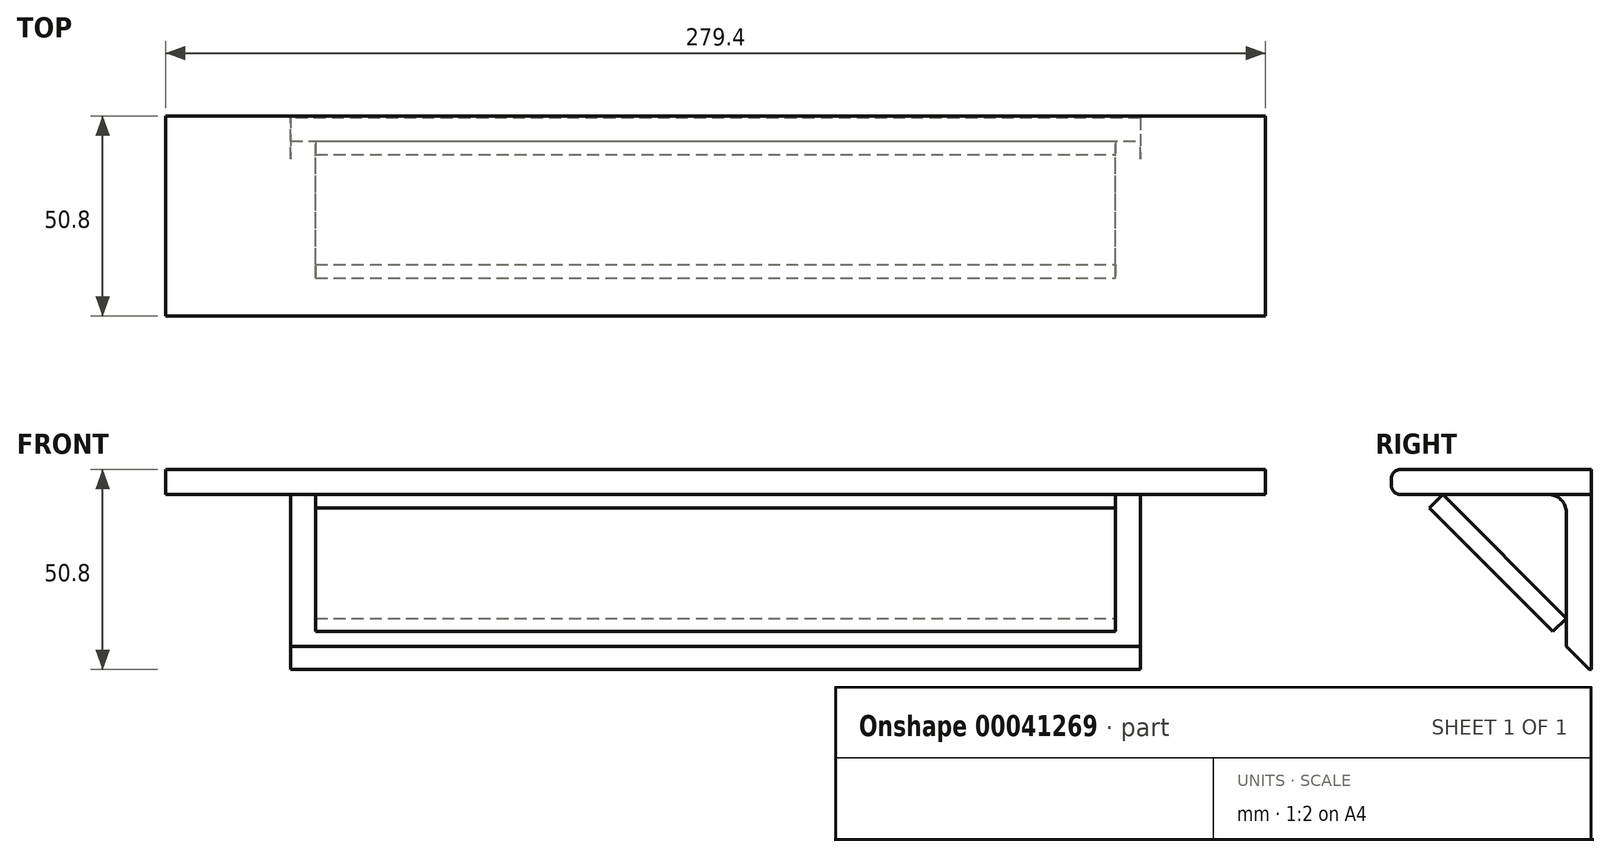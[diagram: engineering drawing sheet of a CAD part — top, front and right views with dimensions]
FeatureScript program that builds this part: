
annotation { "Feature Type Name" : "Feature", "Feature Type Description" : "" }
export const myFeature = defineFeature(function(context is Context, id is Id, definition is map)
    precondition{}
    {
        {
            var Q0;
            Q0=qCreatedBy(makeId("Right.planeOp"),FACE);
            var sketch = newSketch(context, id + "F0", { "sketchPlane" : qUnion([Q0])});
            skLineSegment(sketch, "E0", {"start": v(0, 0) * mm, "end": v(50.8, 0) * mm});
            skLineSegment(sketch, "E1", {"start": v(50.8, 0) * mm, "end": v(50.8, -50.8) * mm});
            skLineSegment(sketch, "E2", {"start": v(50.8, -50.8) * mm, "end": v(44.45, -50.8) * mm});
            skLineSegment(sketch, "E3", {"start": v(44.45, -50.8) * mm, "end": v(44.45, -6.35) * mm});
            skLineSegment(sketch, "E4", {"start": v(44.45, -6.35) * mm, "end": v(0, -6.35) * mm});
            skLineSegment(sketch, "E5", {"start": v(0, -6.35) * mm, "end": v(0, 0) * mm});
            skSolve(sketch);
        }
        {
            var Q0;
            Q0=makeQuery(id+"F0.imprint","IMPRINT",FACE,{"disambiguationData":[TD([[makeQuery(id+"F0.imprint","IMPRINT",EDGE,{"derivedFrom":sQuery(id+"F0.wireOp",EDGE,"E0")}),-1.0]])]});
            extrude(context, id + "F1", {"entities" : qUnion([Q0]), "oppositeDirection" : true, "depth" : 279.4 * mm});
        }
        {
            var Q0;
            Q0=makeQuery(id+"F1.opExtrude","SWEPT_EDGE",EDGE,{"disambiguationData":[OSD([sQuery(id+"F0.wireOp",EDGE,"E4"),sQuery(id+"F0.wireOp",EDGE,"E5")])]});
            var Q1;
            Q1=makeQuery(id+"F1.opExtrude","SWEPT_EDGE",EDGE,{"disambiguationData":[OSD([sQuery(id+"F0.wireOp",EDGE,"E0"),sQuery(id+"F0.wireOp",EDGE,"E5")])]});
            fillet(context, id + "F2", {"entities" : qUnion([Q0, Q1]), "radius" : 2.36 * mm, "tangentPropagation" : true, "allowEdgeOverflow" : false});
        }
        {
            var Q0;
            Q0=makeQuery(id+"F1.opExtrude","CAP_FACE",FACE,{"disambiguationData":[OSD([sQuery(id+"F0.wireOp",EDGE,"E0"),sQuery(id+"F0.wireOp",EDGE,"E1"),sQuery(id+"F0.wireOp",EDGE,"E2"),sQuery(id+"F0.wireOp",EDGE,"E3"),sQuery(id+"F0.wireOp",EDGE,"E4"),sQuery(id+"F0.wireOp",EDGE,"E5")])],"isStart":true});
            var sketch = newSketch(context, id + "F3", { "sketchPlane" : qUnion([Q0])});
            skLineSegment(sketch, "E6", {"start": v(13.02, -6.35) * mm, "end": v(44.45, -37.78) * mm});
            skLineSegment(sketch, "E7", {"start": v(44.45, -37.78) * mm, "end": v(41.08, -41.15) * mm});
            skLineSegment(sketch, "E8", {"start": v(41.08, -41.15) * mm, "end": v(9.65, -9.72) * mm});
            skLineSegment(sketch, "E9", {"start": v(9.65, -9.72) * mm, "end": v(13.02, -6.35) * mm});
            skSolve(sketch);
        }
        {
            var Q0;
            Q0=makeQuery(id+"F3.imprint","IMPRINT",FACE,{"disambiguationData":[TD([[makeQuery(id+"F3.imprint","IMPRINT",EDGE,{"derivedFrom":sQuery(id+"F3.wireOp",EDGE,"E6")}),-1.0]])]});
            extrude(context, id + "F4", {"entities" : qUnion([Q0]), "oppositeDirection" : true, "depth" : 279.4 * mm});
        }
        {
            var Q0;
            Q0=makeQuery(id+"F4.opExtrude","SWEPT_FACE",FACE,{"disambiguationData":[OSD([sQuery(id+"F3.wireOp",EDGE,"E8")])]});
            var sketch = newSketch(context, id + "F5", { "sketchPlane" : qUnion([Q0])});
            skLineSegment(sketch, "E10.bottom", {"start": v(-279.4, -13.7) * mm, "end": v(-241.3, -13.7) * mm});
            skLineSegment(sketch, "E10.top", {"start": v(-279.4, -58.15) * mm, "end": v(-241.3, -58.15) * mm});
            skLineSegment(sketch, "E10.left", {"start": v(-279.4, -13.7) * mm, "end": v(-279.4, -58.15) * mm});
            skLineSegment(sketch, "E10.right", {"start": v(-241.3, -13.7) * mm, "end": v(-241.3, -58.15) * mm});
            skSolve(sketch);
        }
        {
            var Q0;
            Q0=makeQuery(id+"F5.imprint","IMPRINT",FACE,{"disambiguationData":[TD([[makeQuery(id+"F5.imprint","IMPRINT",EDGE,{"derivedFrom":sQuery(id+"F5.wireOp",EDGE,"E10.bottom")}),-1.0]])]});
            extrude(context, id + "F6", {"entities" : qUnion([Q0]), "operationType" : NewBodyOperationType.REMOVE, "oppositeDirection" : true, "depth" : 4.76 * mm});
        }
        {
            var Q0;
            Q0=makeQuery(id+"F4.opExtrude","SWEPT_FACE",FACE,{"disambiguationData":[OSD([sQuery(id+"F3.wireOp",EDGE,"E8")])]});
            var sketch = newSketch(context, id + "F7", { "sketchPlane" : qUnion([Q0])});
            skLineSegment(sketch, "E11.bottom", {"start": v(0, -13.7) * mm, "end": v(-38.1, -13.7) * mm});
            skLineSegment(sketch, "E11.top", {"start": v(0, -58.15) * mm, "end": v(-38.1, -58.15) * mm});
            skLineSegment(sketch, "E11.left", {"start": v(0, -13.7) * mm, "end": v(0, -58.15) * mm});
            skLineSegment(sketch, "E11.right", {"start": v(-38.1, -13.7) * mm, "end": v(-38.1, -58.15) * mm});
            skSolve(sketch);
        }
        {
            var Q0;
            Q0 = qSketchRegion(id + "F7", true);
            extrude(context, id + "F8", {"entities" : qUnion([Q0]), "operationType" : NewBodyOperationType.REMOVE, "oppositeDirection" : true, "depth" : 4.76 * mm});
        }
        {
            var Q0;
            Q0=makeQuery(id+"F1.opExtrude","SWEPT_FACE",FACE,{"disambiguationData":[OSD([sQuery(id+"F0.wireOp",EDGE,"E3")])]});
            var sketch = newSketch(context, id + "F9", { "sketchPlane" : qUnion([Q0])});
            skLineSegment(sketch, "E12.bottom", {"start": v(0, -6.35) * mm, "end": v(-31.75, -6.35) * mm});
            skLineSegment(sketch, "E12.top", {"start": v(0, -57.15) * mm, "end": v(-31.75, -57.15) * mm});
            skLineSegment(sketch, "E12.left", {"start": v(0, -6.35) * mm, "end": v(0, -57.15) * mm});
            skLineSegment(sketch, "E12.right", {"start": v(-31.75, -6.35) * mm, "end": v(-31.75, -57.15) * mm});
            skSolve(sketch);
        }
        {
            var Q0;
            {var subQ6=sQuery(id+"F9.wireOp",EDGE,"E12.bottom");Q0=makeQuery(id+"F9.imprint","IMPRINT",FACE,{"disambiguationData":[TD([[makeQuery(id+"F9.imprint","IMPRINT",EDGE,{"derivedFrom":subQ6}),-1.0]])]});}
            extrude(context, id + "F10", {"entities" : qUnion([Q0]), "operationType" : NewBodyOperationType.REMOVE, "oppositeDirection" : true, "depth" : 25.4 * mm});
        }
        {
            var Q0;
            Q0=makeQuery(id+"F1.opExtrude","SWEPT_FACE",FACE,{"disambiguationData":[OSD([sQuery(id+"F0.wireOp",EDGE,"E3")])]});
            var sketch = newSketch(context, id + "F11", { "sketchPlane" : qUnion([Q0])});
            skLineSegment(sketch, "E13.bottom", {"start": v(-279.4, -6.35) * mm, "end": v(-247.65, -6.35) * mm});
            skLineSegment(sketch, "E13.top", {"start": v(-279.4, -57.15) * mm, "end": v(-247.65, -57.15) * mm});
            skLineSegment(sketch, "E13.left", {"start": v(-279.4, -6.35) * mm, "end": v(-279.4, -57.15) * mm});
            skLineSegment(sketch, "E13.right", {"start": v(-247.65, -6.35) * mm, "end": v(-247.65, -57.15) * mm});
            skSolve(sketch);
        }
        {
            var Q0;
            Q0 = qSketchRegion(id + "F11", true);
            extrude(context, id + "F12", {"entities" : qUnion([Q0]), "operationType" : NewBodyOperationType.REMOVE, "oppositeDirection" : true, "depth" : 25.4 * mm});
        }
        {
            var Q0;
            Q0=makeQuery(id+"F1.opExtrude","SWEPT_EDGE",EDGE,{"disambiguationData":[OSD([sQuery(id+"F0.wireOp",EDGE,"E3"),sQuery(id+"F0.wireOp",EDGE,"E4")])]});
            fillet(context, id + "F13", {"entities" : qUnion([Q0]), "radius" : 4.57 * mm, "tangentPropagation" : true, "allowEdgeOverflow" : false});
        }
        {
            var Q0;
            Q0=makeQuery(id+"F1.opExtrude","SWEPT_EDGE",EDGE,{"disambiguationData":[OSD([sQuery(id+"F0.wireOp",EDGE,"E2"),sQuery(id+"F0.wireOp",EDGE,"E3")])]});
            chamfer(context, id + "F14", {"entities" : qUnion([Q0]), "width" : 5.84 * mm, "tangentPropagation" : true});
        }
    });
